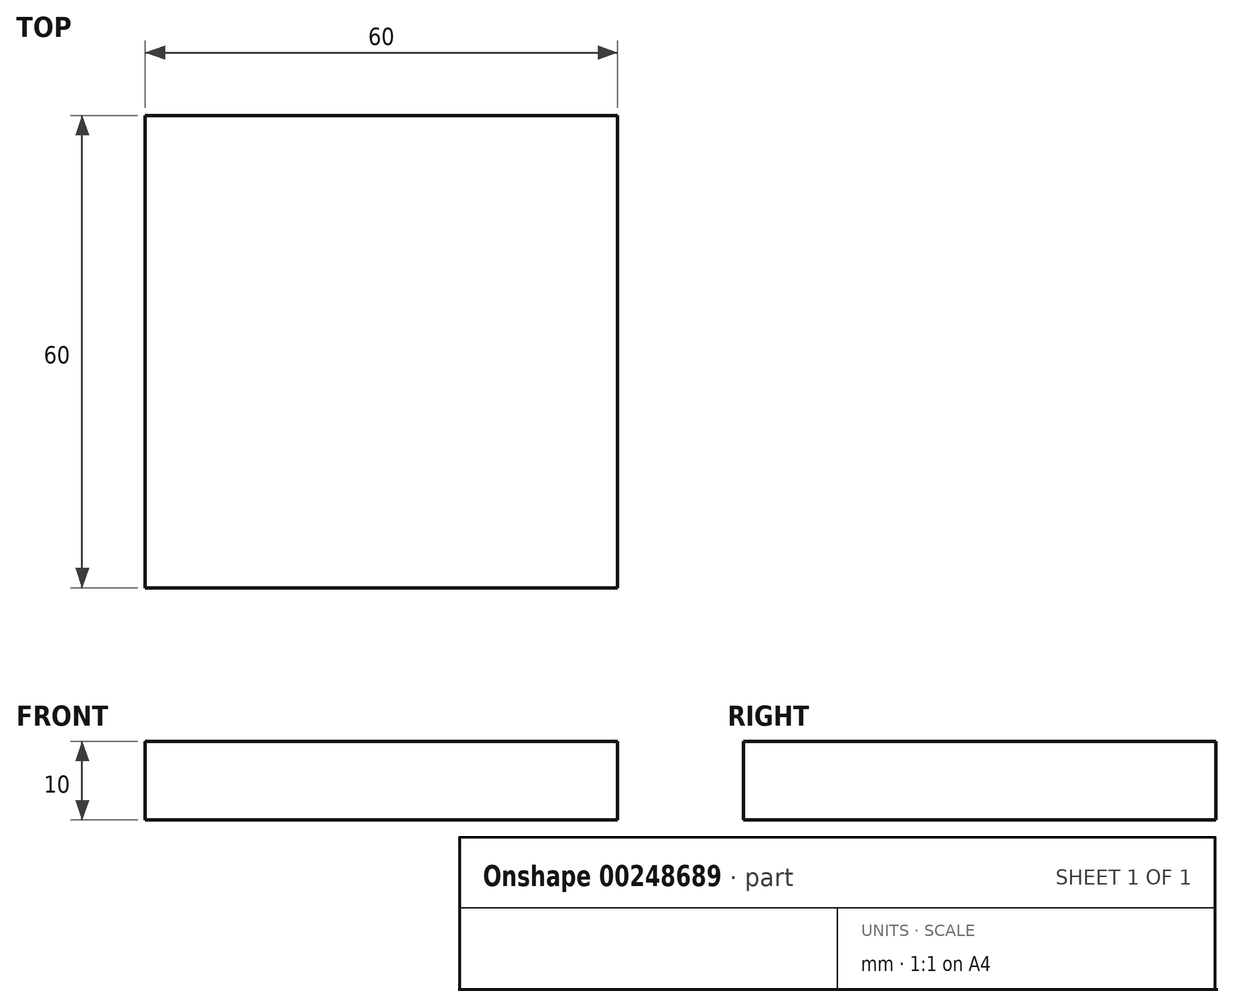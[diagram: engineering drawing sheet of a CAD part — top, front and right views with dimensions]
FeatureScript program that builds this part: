
annotation { "Feature Type Name" : "Feature", "Feature Type Description" : "" }
export const myFeature = defineFeature(function(context is Context, id is Id, definition is map)
    precondition{}
    {
        {
            var Q0;
            Q0=qCreatedBy(makeId("Top.planeOp"),FACE);
            var sketch = newSketch(context, id + "F0", { "sketchPlane" : qUnion([Q0])});
            skLineSegment(sketch, "E0.bottom", {"start": v(30, -34.37) * mm, "end": v(-30, -34.37) * mm});
            skLineSegment(sketch, "E0.top", {"start": v(30, 25.63) * mm, "end": v(-30, 25.63) * mm});
            skLineSegment(sketch, "E0.left", {"start": v(30, -34.37) * mm, "end": v(30, 25.63) * mm});
            skLineSegment(sketch, "E0.right", {"start": v(-30, -34.37) * mm, "end": v(-30, 25.63) * mm});
            skPoint(sketch, "E0.middle", {"position": v(0, -4.37) * mm});
            skSolve(sketch);
        }
        {
            var Q0;
            Q0=makeQuery(id+"F0.imprint","IMPRINT",FACE,{"disambiguationData":[TD([[makeQuery(id+"F0.imprint","IMPRINT",EDGE,{"derivedFrom":sQuery(id+"F0.wireOp",EDGE,"E0.bottom")}),-1.0]])]});
            extrude(context, id + "F1", {"entities" : qUnion([Q0]), "depth" : 10 * mm});
        }
    });
